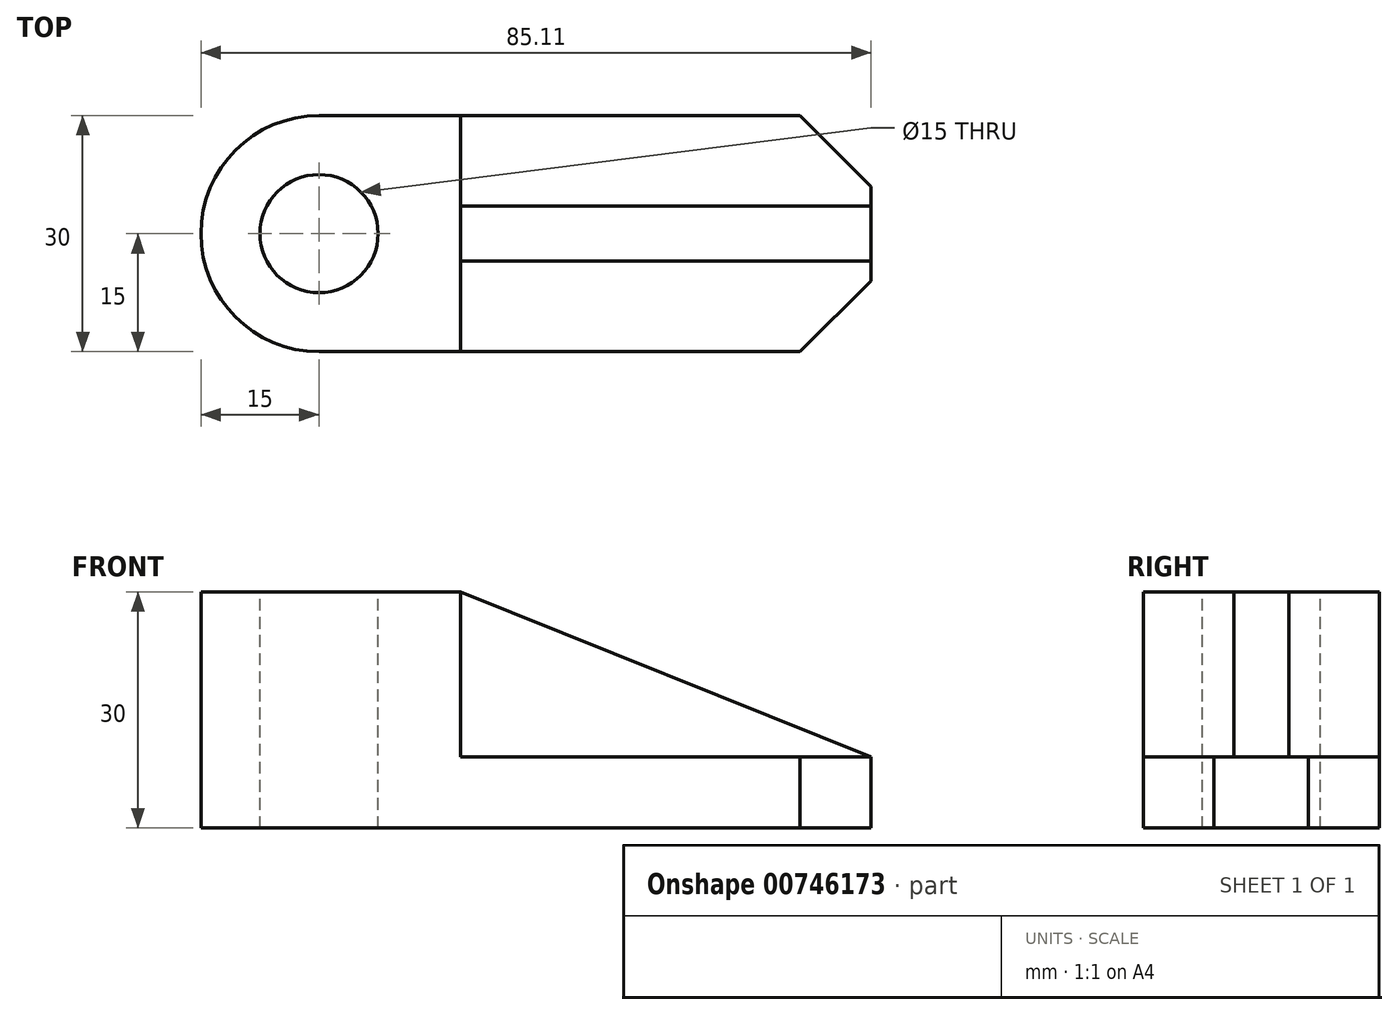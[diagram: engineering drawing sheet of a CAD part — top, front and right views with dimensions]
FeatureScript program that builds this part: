
annotation { "Feature Type Name" : "Feature", "Feature Type Description" : "" }
export const myFeature = defineFeature(function(context is Context, id is Id, definition is map)
    precondition{}
    {
        {
            var Q0;
            Q0=qCreatedBy(makeId("Top.planeOp"),FACE);
            var sketch = newSketch(context, id + "F0", { "sketchPlane" : qUnion([Q0])});
            skLineSegment(sketch, "E0", {"start": v(0, 0) * mm, "end": v(61.1, 0) * mm});
            skLineSegment(sketch, "E1", {"start": v(61.1, 0) * mm, "end": v(70.1, -9) * mm});
            skLineSegment(sketch, "E2", {"start": v(70.1, -9) * mm, "end": v(70.1, -21) * mm});
            skLineSegment(sketch, "E3", {"start": v(70.1, -21) * mm, "end": v(61.1, -30) * mm});
            skLineSegment(sketch, "E4", {"start": v(61.1, -30) * mm, "end": v(0, -30) * mm});
            skArc(sketch, "E5", {"start": v(0, 0) * mm, "mid": v(-15, -15) * mm, "end": v(0, -30) * mm});
            skSolve(sketch);
        }
        {
            var Q0;
            Q0=makeQuery(id+"F0.imprint","IMPRINT",FACE,{"disambiguationData":[TD([[makeQuery(id+"F0.imprint","IMPRINT",EDGE,{"derivedFrom":sQuery(id+"F0.wireOp",EDGE,"E0")}),-1.0]])]});
            extrude(context, id + "F1", {"entities" : qUnion([Q0]), "depth" : 9 * mm, "offsetDistance" : 25 * mm});
        }
        {
            var Q0;
            Q0=makeQuery(id+"F1.opExtrude","CAP_FACE",FACE,{"disambiguationData":[OSD([sQuery(id+"F0.wireOp",EDGE,"E0"),sQuery(id+"F0.wireOp",EDGE,"E1"),sQuery(id+"F0.wireOp",EDGE,"E2"),sQuery(id+"F0.wireOp",EDGE,"E3"),sQuery(id+"F0.wireOp",EDGE,"E4"),sQuery(id+"F0.wireOp",EDGE,"E5")])],"isStart":false});
            var sketch = newSketch(context, id + "F2", { "sketchPlane" : qUnion([Q0])});
            skLineSegment(sketch, "E6", {"start": v(18, 0) * mm, "end": v(18, -30) * mm});
            skSolve(sketch);
        }
        {
            var Q0;
            Q0 = qSketchRegion(id + "F2", true);
            var Q1;
            {var subQ0=sQuery(id+"F2.wireOp",EDGE,"E6");Q1=makeQuery(id+"F2.imprint","IMPRINT",FACE,{"disambiguationData":[TD([[makeQuery(id+"F2.imprint","IMPRINT",EDGE,{"derivedFrom":subQ0}),-1.0]])]});}
            extrude(context, id + "F3", {"entities" : qUnion([Q0, Q1]), "operationType" : NewBodyOperationType.ADD, "depth" : 21 * mm, "offsetDistance" : 25 * mm});
        }
        {
            var Q0;
            Q0=makeQuery(id+"F3.opExtrude","CAP_FACE",FACE,{"disambiguationData":[OSD([sQuery(id+"F0.wireOp",EDGE,"E0"),sQuery(id+"F0.wireOp",EDGE,"E4"),sQuery(id+"F0.wireOp",EDGE,"E5"),sQuery(id+"F2.wireOp",EDGE,"E6")])],"isStart":false});
            var sketch = newSketch(context, id + "F4", { "sketchPlane" : qUnion([Q0])});
            skCircle(sketch, "E7", {"center": v(0, -15) * mm, "radius": 7.5 * mm});
            skSolve(sketch);
        }
        {
            var Q0;
            Q0 = qSketchRegion(id + "F4", true);
            extrude(context, id + "F5", {"entities" : qUnion([Q0]), "operationType" : NewBodyOperationType.REMOVE, "oppositeDirection" : true, "depth" : 37.3 * mm, "offsetDistance" : 25 * mm});
        }
        {
            var Q0;
            Q0=makeQuery(id+"F1.opExtrude","CAP_FACE",FACE,{"disambiguationData":[OSD([sQuery(id+"F0.wireOp",EDGE,"E0"),sQuery(id+"F0.wireOp",EDGE,"E1"),sQuery(id+"F0.wireOp",EDGE,"E2"),sQuery(id+"F0.wireOp",EDGE,"E3"),sQuery(id+"F0.wireOp",EDGE,"E4"),sQuery(id+"F0.wireOp",EDGE,"E5")])],"isStart":false});
            var sketch = newSketch(context, id + "F6", { "sketchPlane" : qUnion([Q0])});
            skLineSegment(sketch, "E8", {"start": v(70.1, -11.5) * mm, "end": v(18, -11.5) * mm});
            skLineSegment(sketch, "E9", {"start": v(18, -11.5) * mm, "end": v(18, -18.5) * mm});
            skLineSegment(sketch, "E10", {"start": v(18, -18.5) * mm, "end": v(70.1, -18.5) * mm});
            skLineSegment(sketch, "E11", {"start": v(70.1, -18.5) * mm, "end": v(70.1, -11.5) * mm});
            skSolve(sketch);
        }
        {
            var Q0;
            Q0=makeQuery(id+"F6.imprint","IMPRINT",FACE,{"disambiguationData":[TD([[makeQuery(id+"F6.imprint","IMPRINT",EDGE,{"derivedFrom":sQuery(id+"F6.wireOp",EDGE,"E8")}),1.0]])]});
            extrude(context, id + "F7", {"entities" : qUnion([Q0]), "operationType" : NewBodyOperationType.ADD, "depth" : 21 * mm, "offsetDistance" : 25 * mm});
        }
        {
            var Q0;
            Q0=makeQuery(id+"F7.opExtrude","SWEPT_FACE",FACE,{"disambiguationData":[OSD([sQuery(id+"F6.wireOp",EDGE,"E10")])]});
            var sketch = newSketch(context, id + "F8", { "sketchPlane" : qUnion([Q0])});
            skLineSegment(sketch, "E12", {"start": v(18, 30) * mm, "end": v(70.1, 9) * mm});
            skLineSegment(sketch, "E13", {"start": v(70.1, 9) * mm, "end": v(70.1, 30) * mm});
            skLineSegment(sketch, "E14", {"start": v(70.1, 30) * mm, "end": v(18, 30) * mm});
            skSolve(sketch);
        }
        {
            var Q0;
            Q0 = qSketchRegion(id + "F8", true);
            extrude(context, id + "F9", {"entities" : qUnion([Q0]), "operationType" : NewBodyOperationType.REMOVE, "oppositeDirection" : true, "depth" : 25 * mm, "offsetDistance" : 25 * mm});
        }
    });
